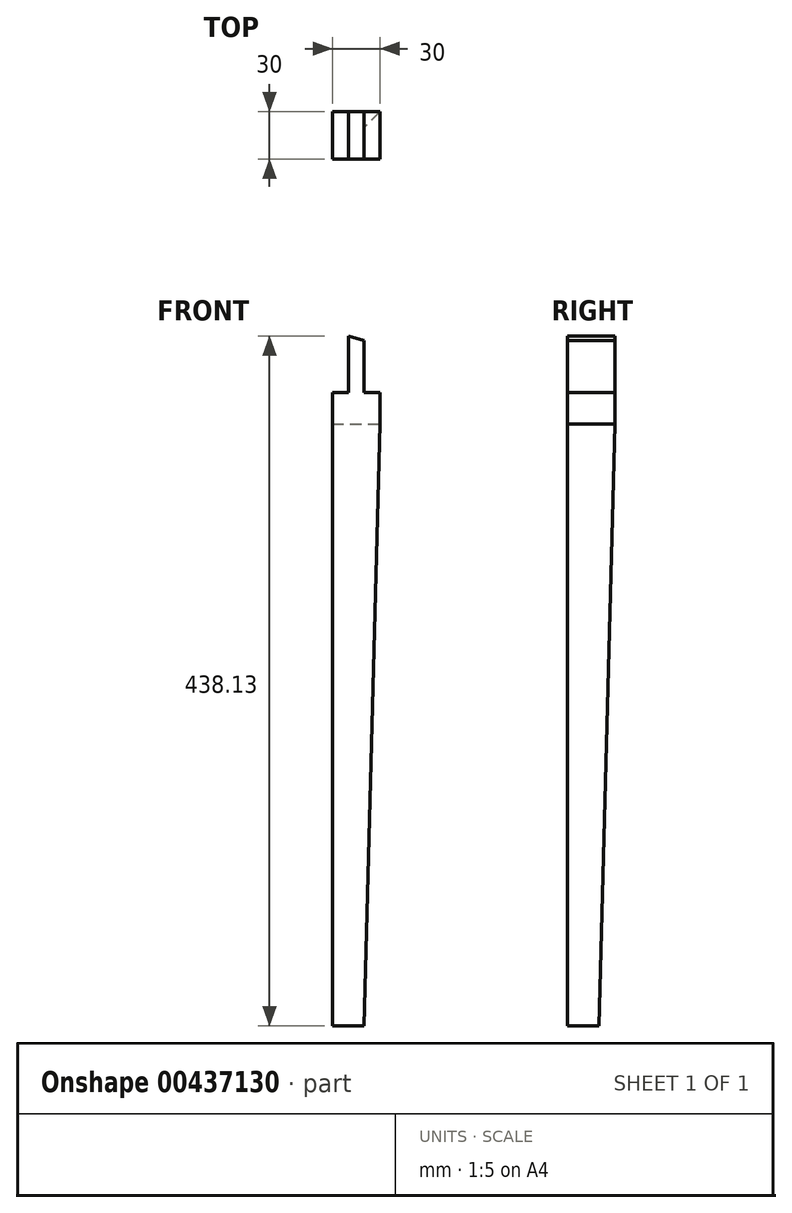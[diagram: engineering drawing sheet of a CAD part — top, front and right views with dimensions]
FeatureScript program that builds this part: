
annotation { "Feature Type Name" : "Feature", "Feature Type Description" : "" }
export const myFeature = defineFeature(function(context is Context, id is Id, definition is map)
    precondition{}
    {
        {
            var Q0;
            Q0=qCreatedBy(makeId("Front.planeOp"),FACE);
            var sketch = newSketch(context, id + "F0", { "sketchPlane" : qUnion([Q0])});
            skLineSegment(sketch, "E0", {"start": v(0, 0) * mm, "end": v(0, 441) * mm});
            skLineSegment(sketch, "E1", {"start": v(0, 0) * mm, "end": v(20, 0) * mm});
            skLineSegment(sketch, "E2", {"start": v(0, 441) * mm, "end": v(30, 432.4) * mm});
            skLineSegment(sketch, "E3", {"start": v(30, 432.4) * mm, "end": v(30, 382.4) * mm});
            skLineSegment(sketch, "E4", {"start": v(30, 382.4) * mm, "end": v(20, 0) * mm});
            skSolve(sketch);
        }
        {
            var Q0;
            Q0 = qSketchRegion(id + "F0", true);
            extrude(context, id + "F1", {"entities" : qUnion([Q0]), "depth" : 30 * mm});
        }
        {
            var Q0;
            Q0=makeQuery(id+"F1.opExtrude","SWEPT_FACE",FACE,{"disambiguationData":[OSD([sQuery(id+"F0.wireOp",EDGE,"E0")])]});
            var sketch = newSketch(context, id + "F2", { "sketchPlane" : qUnion([Q0])});
            skLineSegment(sketch, "E5", {"start": v(0, 0) * mm, "end": v(10, 0) * mm});
            skLineSegment(sketch, "E6", {"start": v(10, 0) * mm, "end": v(0, 382.06) * mm});
            skLineSegment(sketch, "E7", {"start": v(0, 382.06) * mm, "end": v(0, 0) * mm});
            skSolve(sketch);
        }
        {
            var Q0;
            Q0 = qSketchRegion(id + "F2", true);
            extrude(context, id + "F3", {"entities" : qUnion([Q0]), "operationType" : NewBodyOperationType.REMOVE, "oppositeDirection" : true, "depth" : 30 * mm});
        }
        {
            var Q0;
            Q0=makeQuery(id+"F1.opExtrude","CAP_FACE",FACE,{"disambiguationData":[OSD([sQuery(id+"F0.wireOp",EDGE,"E0"),sQuery(id+"F0.wireOp",EDGE,"E1"),sQuery(id+"F0.wireOp",EDGE,"E2"),sQuery(id+"F0.wireOp",EDGE,"E3"),sQuery(id+"F0.wireOp",EDGE,"E4")])],"isStart":false});
            var sketch = newSketch(context, id + "F4", { "sketchPlane" : qUnion([Q0])});
            skLineSegment(sketch, "E8", {"start": v(30, 432.4) * mm, "end": v(30, 402.4) * mm});
            skLineSegment(sketch, "E9", {"start": v(30, 402.4) * mm, "end": v(20, 402.4) * mm});
            skLineSegment(sketch, "E10", {"start": v(20, 402.4) * mm, "end": v(20, 435.27) * mm});
            skLineSegment(sketch, "E11", {"start": v(20, 435.27) * mm, "end": v(30, 432.4) * mm});
            skLineSegment(sketch, "E12", {"start": v(0, 402.4) * mm, "end": v(10, 402.4) * mm});
            skLineSegment(sketch, "E13", {"start": v(0, 402.4) * mm, "end": v(0, 441) * mm});
            skLineSegment(sketch, "E14", {"start": v(10, 402.4) * mm, "end": v(10, 438.13) * mm});
            skLineSegment(sketch, "E15", {"start": v(10, 438.13) * mm, "end": v(0, 441) * mm});
            skSolve(sketch);
        }
        {
            var Q0;
            Q0 = qSketchRegion(id + "F4", true);
            extrude(context, id + "F5", {"entities" : qUnion([Q0]), "operationType" : NewBodyOperationType.REMOVE, "oppositeDirection" : true, "depth" : 30 * mm});
        }
    });
